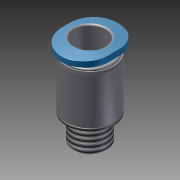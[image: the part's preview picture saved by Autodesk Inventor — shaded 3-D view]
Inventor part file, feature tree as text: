
AUTODESK INVENTOR PART (.ipt)
format: ipt  version: 2014 (Build 180170000, 170)  size: 199,680 bytes
history: native  units: mm
features: other x21, sketch x4, revolve x2, extrude x2, thread x1
ambient origin geometry x8: Origin, YZ Plane, XZ Plane, XY Plane, X Axis, Y Axis, Z Axis, Center Point
bodies: Solid1 (feature_tree)
feature tree (30):
  revolve  "Revolution1"  [1 undecoded]
  thread  "Thread1"  [1 undecoded]
  extrude  "Extrusion1"  TaperAngle=360.0deg  [1 undecoded]
  extrude  "Extrusion2"  [1 undecoded]
  revolve  "Revolution2"  [1 undecoded]
  other  "ANBAU_XY"
  other  "ANBAU_YZ"
  other  "ANBAU_ZX"
  other  "ANBAU_X"
  other  "ANBAU_Y"
  other  "ANBAU_Z"
  other  "ANBAU_Center"
  other  "CPV_XY"
  other  "CPV_YZ"
  other  "CPV_ZX"
  other  "CPV_X"
  other  "CPV_Y"
  other  "CPV_Z"
  other  "CPV_Center"
  other  "CPV_ANBAU_XY"
  other  "CPV_ANBAU_YZ"
  other  "CPV_ANBAU_ZX"
  other  "CPV_ANBAU_X"
  other  "CPV_ANBAU_Y"
  other  "CPV_ANBAU_Z"
  other  "CPV_ANBAU_Center"
  sketch  "Sketch_1"  dims[d0=360.0deg d1=4.3865mm d2=0.0mm d3=1.5mm d4=0.0mm]
  sketch  "Sketch_2"  dims[d5=7.2mm d6=0.0mm d7=360.0deg]
  sketch  "Sketch_3"
  sketch  "Sketch_4"
note: 5 required parameter values undecoded (feature->parameter linkage not recoverable at this tier; creation-order binding heuristic only, values carry confidence <= 0.55)